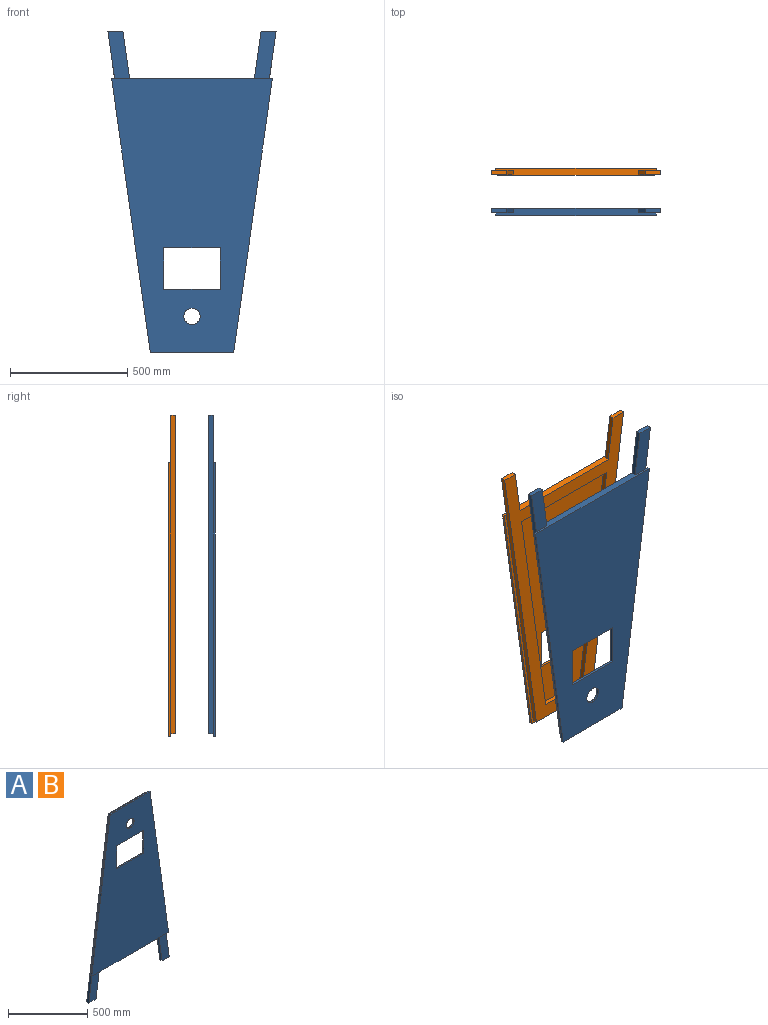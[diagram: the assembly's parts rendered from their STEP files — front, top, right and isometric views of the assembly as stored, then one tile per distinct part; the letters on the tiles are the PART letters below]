
ASSEMBLY  parts=2 mates=4
PART A: 26 faces, bbox 717.4x28.6x1370.8 mm
  f0: plane 1028.7x513.94mm, normal (0,1,0), area 332423.8mm2, adj f1,f2,f3,f7,f9,f20,f21,f22
  f1: plane 241.3x9.53mm, normal (0,0,-1), area 2298.4mm2, adj f0,f2,f9,f10
  f2: plane 177.8x9.53mm, normal (-1,0,0), area 1693.5mm2, adj f0,f1,f3,f10
  f3: plane 241.3x9.53mm, normal (0,0,1), area 2298.4mm2, adj f0,f2,f9,f10
  f4: plane 1168.4x165.1mm, normal (-0.99,0,0.14), area 11239.6mm2, adj f5,f8,f10,f11
  f5: plane 685.8x28.58mm, normal (0,0,-1), area 16664.7mm2, adj f4,f6,f10,f11,f12,f13,f17,f18
  f6: plane 1168.4x165.1mm, normal (0.99,0,0.14), area 11239.6mm2, adj f5,f8,f10,f11
  f7: cylinder r=34.92mm len=69.85mm, axis (0,1,0), area 2090.2mm2, adj f0,f10
  f8: plane 355.6x9.53mm, normal (0,0,1), area 3387.1mm2, adj f4,f6,f10,f11
  f9: plane 177.8x9.53mm, normal (1,0,0), area 1693.5mm2, adj f0,f1,f3,f10
  f10: plane 1168.4x685.8mm, normal (0,-1,0), area 561650.8mm2, adj f1,f2,f3,f4,f5,f6,f7,f8
  f11: plane 1168.4x685.8mm, normal (0,1,0), area 34185.3mm2, adj f4,f5,f6,f8,f14,f15,f24
  f12: plane 202.41x92.73mm, normal (0,-1,0), area 12980.6mm2, adj f5,f15,f16,f17
  f13: plane 202.41x92.73mm, normal (0,-1,0), area 12980.6mm2, adj f5,f18,f19,f24
  f14: plane 333.54x19.05mm, normal (0,0,1), area 6353.9mm2, adj f11,f15,f24,f25
  f15: plane 1358.11x191.91mm, normal (0.99,0,0.14), area 26129mm2, adj f11,f12,f14,f16,f25
  f16: plane 64.13x19.05mm, normal (0,0,-1), area 1221.7mm2, adj f12,f15,f17,f25
  f17: plane 202.41x28.6mm, normal (-0.99,0,-0.14), area 3894.2mm2, adj f5,f12,f16,f25
  f18: plane 202.41x28.6mm, normal (0.99,0,-0.14), area 3894.2mm2, adj f5,f13,f19,f25
  f19: plane 64.13x19.05mm, normal (0,0,-1), area 1221.7mm2, adj f13,f18,f24,f25
  f20: plane 1028.7x145.36mm, normal (-0.99,0,-0.14), area 19791.4mm2, adj f0,f21,f23,f25
  f21: plane 223.22x19.05mm, normal (0,0,-1), area 4252.4mm2, adj f0,f20,f22,f25
  f22: plane 1028.7x145.36mm, normal (0.99,0,-0.14), area 19791.4mm2, adj f0,f21,f23,f25
  f23: plane 513.94x19.05mm, normal (0,0,1), area 9790.6mm2, adj f0,f20,f22,f25
  f24: plane 1358.11x191.91mm, normal (-0.99,0,0.14), area 26129mm2, adj f11,f13,f14,f19,f25
  f25: plane 1358.11x717.35mm, normal (0,1,0), area 221002.9mm2, adj f5,f14,f15,f16,f17,f18,f19,f20
PART B: same geometry as A
PLACE A rot(axis=(0,1,0),180deg) t=(257.85,642.49,1278.3)mm
PLACE B rot(axis=(1,0,0),180deg) t=(257.85,823.34,1278.3)mm
MATE parallel B.f10 <-> A.f10  axis (0,1,0) through (-2.5,832.87,694.1)mm
MATE planar A.f14 <-> B.f14  axis (0,0,-1) through (257.85,652.02,122.6)mm
MATE planar A.f24 <-> B.f15  axis (0.99,0,-0.14) through (520.57,652.02,801.66)mm
MATE parallel A.f14 <-> B.f14  axis (0,0,-1) through (257.85,652.02,122.6)mm
